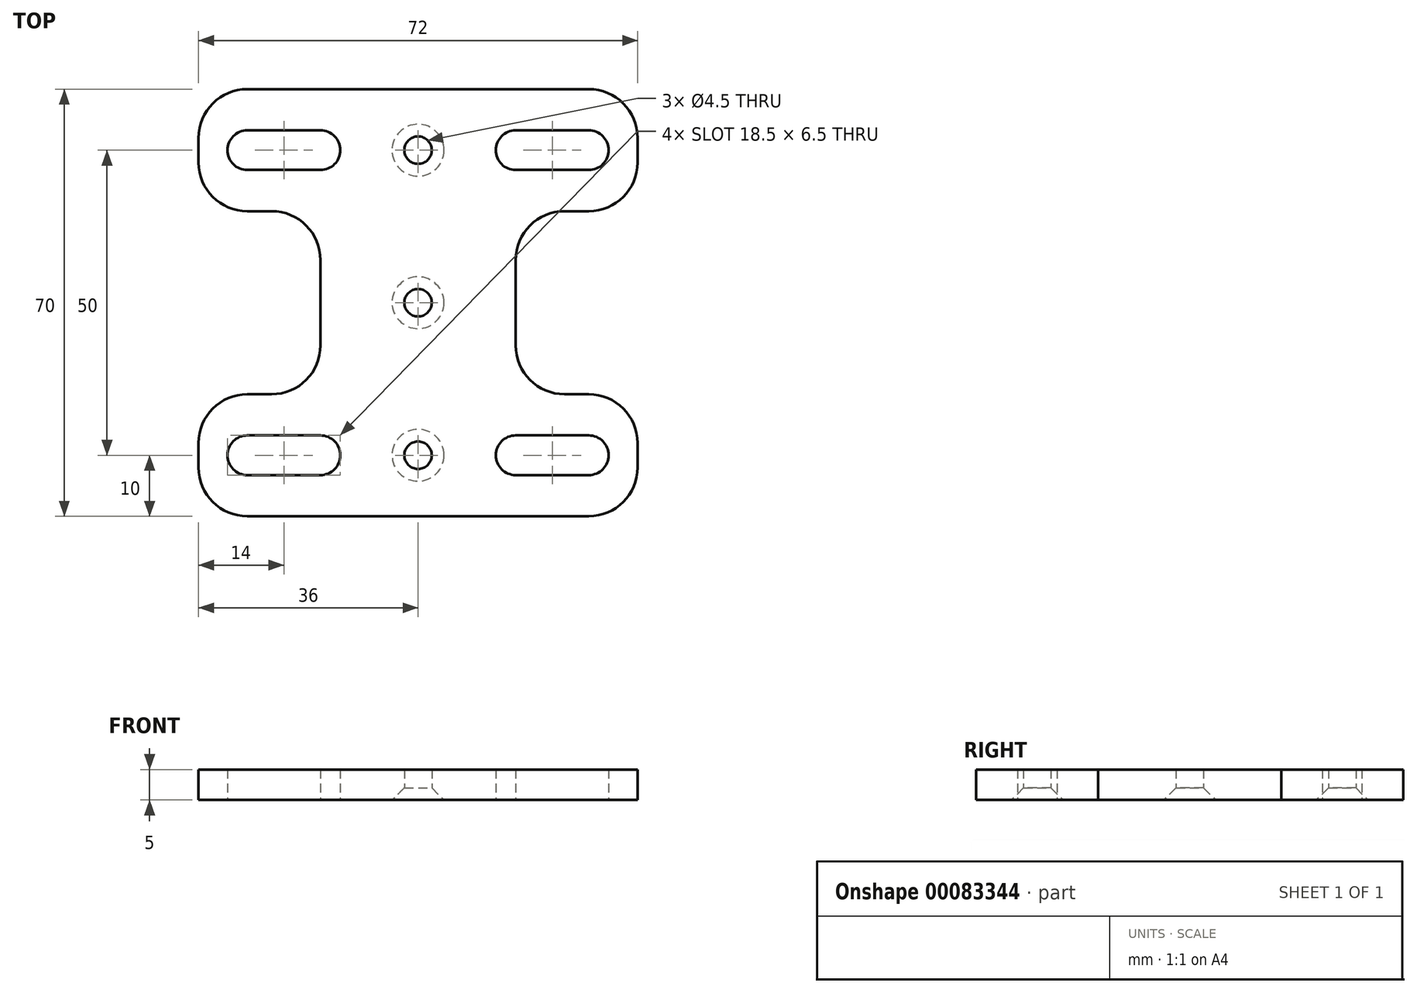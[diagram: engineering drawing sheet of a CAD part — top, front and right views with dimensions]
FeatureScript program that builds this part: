
annotation { "Feature Type Name" : "Feature", "Feature Type Description" : "" }
export const myFeature = defineFeature(function(context is Context, id is Id, definition is map)
    precondition{}
    {
        {
            var Q0;
            Q0=qCreatedBy(makeId("Front.planeOp"),FACE);
            var sketch = newSketch(context, id + "F0", { "sketchPlane" : qUnion([Q0])});
            skLineSegment(sketch, "E0", {"start": v(-14.14, 0) * mm, "end": v(0, -14.14) * mm, "construction": true});
            skLineSegment(sketch, "E1", {"start": v(0, -14.14) * mm, "end": v(14.14, 0) * mm, "construction": true});
            skLineSegment(sketch, "E2", {"start": v(14.14, 0) * mm, "end": v(-14.14, 0) * mm, "construction": true});
            skLineSegment(sketch, "E3", {"start": v(-14.14, 0) * mm, "end": v(0, 14.14) * mm, "construction": true});
            skLineSegment(sketch, "E4", {"start": v(0, 14.14) * mm, "end": v(14.14, 0) * mm, "construction": true});
            skLineSegment(sketch, "E5.0", {"start": v(14.14, -0.03) * mm, "end": v(-14.14, -0.03) * mm, "construction": true});
            skSolve(sketch);
        }
        {
            var Q0;
            Q0=qCreatedBy(makeId("Top.planeOp"),FACE);
            var sketch = newSketch(context, id + "F1", { "sketchPlane" : qUnion([Q0])});
            skLineSegment(sketch, "E6.bottom", {"start": v(-16, 25) * mm, "end": v(16, 25) * mm, "construction": true});
            skLineSegment(sketch, "E6.top", {"start": v(-16, -25) * mm, "end": v(16, -25) * mm, "construction": true});
            skLineSegment(sketch, "E6.left", {"start": v(-16, 25) * mm, "end": v(-16, -25) * mm, "construction": true});
            skLineSegment(sketch, "E6.right", {"start": v(16, 25) * mm, "end": v(16, -25) * mm, "construction": true});
            skCircle(sketch, "E7", {"center": v(-16, 25) * mm, "radius": 3.25 * mm});
            skCircle(sketch, "E8", {"center": v(16, 25) * mm, "radius": 3.25 * mm});
            skCircle(sketch, "E9", {"center": v(-16, -25) * mm, "radius": 3.25 * mm});
            skCircle(sketch, "E10", {"center": v(16, -25) * mm, "radius": 3.25 * mm});
            skLineSegment(sketch, "E11", {"start": v(-36, 35) * mm, "end": v(36, 35) * mm});
            skLineSegment(sketch, "E12", {"start": v(36, 35) * mm, "end": v(36, -35) * mm});
            skLineSegment(sketch, "E13", {"start": v(36, -35) * mm, "end": v(-36, -35) * mm});
            skLineSegment(sketch, "E14", {"start": v(-36, 35) * mm, "end": v(-36, -35) * mm});
            skLineSegment(sketch, "E15", {"start": v(-16, 25) * mm, "end": v(-28, 25) * mm, "construction": true});
            skLineSegment(sketch, "E16", {"start": v(-16, -25) * mm, "end": v(-28, -25) * mm, "construction": true});
            skLineSegment(sketch, "E17", {"start": v(16, -25) * mm, "end": v(28, -25) * mm, "construction": true});
            skLineSegment(sketch, "E18", {"start": v(16, 25) * mm, "end": v(28, 25) * mm, "construction": true});
            skCircle(sketch, "E19", {"center": v(-28, 25) * mm, "radius": 3.25 * mm});
            skCircle(sketch, "E20", {"center": v(-28, -25) * mm, "radius": 3.25 * mm});
            skCircle(sketch, "E21", {"center": v(28, -25) * mm, "radius": 3.25 * mm});
            skCircle(sketch, "E22", {"center": v(28, 25) * mm, "radius": 3.25 * mm});
            skLineSegment(sketch, "E23", {"start": v(-16, 28.25) * mm, "end": v(-28, 28.25) * mm});
            skLineSegment(sketch, "E24", {"start": v(-28, 21.75) * mm, "end": v(-16, 21.75) * mm});
            skLineSegment(sketch, "E25", {"start": v(-28, -21.75) * mm, "end": v(-16, -21.75) * mm});
            skLineSegment(sketch, "E26", {"start": v(-16, -28.25) * mm, "end": v(-28, -28.25) * mm});
            skLineSegment(sketch, "E27", {"start": v(28, -21.75) * mm, "end": v(16, -21.75) * mm});
            skLineSegment(sketch, "E28", {"start": v(16, -28.25) * mm, "end": v(28, -28.25) * mm});
            skLineSegment(sketch, "E29", {"start": v(28, 28.25) * mm, "end": v(16, 28.25) * mm});
            skLineSegment(sketch, "E30", {"start": v(16, 21.75) * mm, "end": v(28, 21.75) * mm});
            skLineSegment(sketch, "E31", {"start": v(0, 35) * mm, "end": v(-12.5, 35) * mm, "construction": true});
            skLineSegment(sketch, "E32", {"start": v(-12.5, 35) * mm, "end": v(-22, 35) * mm, "construction": true});
            skCircle(sketch, "E33", {"center": v(-22, 35) * mm, "radius": 9.5 * mm, "construction": true});
            skPoint(sketch, "E34", {"position": v(0, 25) * mm});
            skPoint(sketch, "E35", {"position": v(0, -25) * mm});
            skPoint(sketch, "E36", {"position": v(0, 0) * mm});
            skLineSegment(sketch, "E37", {"start": v(36, 15) * mm, "end": v(16, 15) * mm});
            skLineSegment(sketch, "E38", {"start": v(16, 15) * mm, "end": v(16, -15) * mm});
            skLineSegment(sketch, "E39", {"start": v(16, -15) * mm, "end": v(36, -15) * mm});
            skLineSegment(sketch, "E40", {"start": v(-36, 15) * mm, "end": v(-16, 15) * mm});
            skLineSegment(sketch, "E41", {"start": v(-16, 15) * mm, "end": v(-16, -15) * mm});
            skLineSegment(sketch, "E42", {"start": v(-16, -15) * mm, "end": v(-36, -15) * mm});
            skSolve(sketch);
        }
        {
            var Q0;
            Q0=makeQuery(id+"F1.imprint","IMPRINT",FACE,{"disambiguationData":[TD([[makeQuery(id+"F1.imprint","IMPRINT",EDGE,{"derivedFrom":sQuery(id+"F1.wireOp",EDGE,"E11")}),-1.0]])]});
            extrude(context, id + "F2", {"entities" : qUnion([Q0]), "depth" : 5 * mm});
        }
        {
            var Q0;
            Q0=sQuery(id+"F1.wireOp",VERTEX,"E34");
            var Q1;
            Q1=sQuery(id+"F1.wireOp",VERTEX,"E36");
            var Q2;
            Q2=sQuery(id+"F1.wireOp",VERTEX,"E35");
            var Q3;
            Q3=makeQuery(id+"F2.opExtrude","SWEPT_BODY",BODY,{"disambiguationData":[OSD([sQuery(id+"F1.wireOp",EDGE,"E7"),sQuery(id+"F1.wireOp",EDGE,"E8"),sQuery(id+"F1.wireOp",EDGE,"E9"),sQuery(id+"F1.wireOp",EDGE,"E10"),sQuery(id+"F1.wireOp",EDGE,"E11"),sQuery(id+"F1.wireOp",EDGE,"E12"),sQuery(id+"F1.wireOp",EDGE,"E13"),sQuery(id+"F1.wireOp",EDGE,"E14"),sQuery(id+"F1.wireOp",EDGE,"E19"),sQuery(id+"F1.wireOp",EDGE,"E20"),sQuery(id+"F1.wireOp",EDGE,"E21"),sQuery(id+"F1.wireOp",EDGE,"E22"),sQuery(id+"F1.wireOp",EDGE,"E23"),sQuery(id+"F1.wireOp",EDGE,"E24"),sQuery(id+"F1.wireOp",EDGE,"E25"),sQuery(id+"F1.wireOp",EDGE,"E26"),sQuery(id+"F1.wireOp",EDGE,"E27"),sQuery(id+"F1.wireOp",EDGE,"E28"),sQuery(id+"F1.wireOp",EDGE,"E29"),sQuery(id+"F1.wireOp",EDGE,"E30")])]});
            hole(context, id + "F3", {"style" : HoleStyle.C_SINK, "endStyle" : HoleEndStyle.THROUGH, "oppositeDirection" : true, "holeDiameter" : 4.5 * mm, "cSinkDiameter" : 8.5 * mm, "cSinkAngle" : 90 * degree, "locations" : qUnion([Q0, Q1, Q2]), "scope" : qUnion([Q3]), "isTappedThrough" : true});
        }
        {
            var Q0;
            Q0=makeQuery(id+"F2.opExtrude","SWEPT_EDGE",EDGE,{"disambiguationData":[OSD([sQuery(id+"F1.wireOp",EDGE,"E11"),sQuery(id+"F1.wireOp",EDGE,"E14")])]});
            var Q1;
            Q1=makeQuery(id+"F2.opExtrude","SWEPT_EDGE",EDGE,{"disambiguationData":[OSD([sQuery(id+"F1.wireOp",EDGE,"E14"),sQuery(id+"F1.wireOp",EDGE,"E42")])]});
            var Q2;
            Q2=makeQuery(id+"F2.opExtrude","SWEPT_EDGE",EDGE,{"disambiguationData":[OSD([sQuery(id+"F1.wireOp",EDGE,"E13"),sQuery(id+"F1.wireOp",EDGE,"E14")])]});
            var Q3;
            Q3=makeQuery(id+"F2.opExtrude","SWEPT_EDGE",EDGE,{"disambiguationData":[OSD([sQuery(id+"F1.wireOp",EDGE,"E12"),sQuery(id+"F1.wireOp",EDGE,"E39")])]});
            var Q4;
            Q4=makeQuery(id+"F2.opExtrude","SWEPT_EDGE",EDGE,{"disambiguationData":[OSD([sQuery(id+"F1.wireOp",EDGE,"E12"),sQuery(id+"F1.wireOp",EDGE,"E13")])]});
            var Q5;
            Q5=makeQuery(id+"F2.opExtrude","SWEPT_EDGE",EDGE,{"disambiguationData":[OSD([sQuery(id+"F1.wireOp",EDGE,"E12"),sQuery(id+"F1.wireOp",EDGE,"E37")])]});
            var Q6;
            Q6=makeQuery(id+"F2.opExtrude","SWEPT_EDGE",EDGE,{"disambiguationData":[OSD([sQuery(id+"F1.wireOp",EDGE,"E11"),sQuery(id+"F1.wireOp",EDGE,"E12")])]});
            var Q7;
            Q7=makeQuery(id+"F2.opExtrude","SWEPT_EDGE",EDGE,{"disambiguationData":[OSD([sQuery(id+"F1.wireOp",EDGE,"E41"),sQuery(id+"F1.wireOp",EDGE,"E42")])]});
            var Q8;
            Q8=makeQuery(id+"F2.opExtrude","SWEPT_EDGE",EDGE,{"disambiguationData":[OSD([sQuery(id+"F1.wireOp",EDGE,"E40"),sQuery(id+"F1.wireOp",EDGE,"E41")])]});
            var Q9;
            Q9=makeQuery(id+"F2.opExtrude","SWEPT_EDGE",EDGE,{"disambiguationData":[OSD([sQuery(id+"F1.wireOp",EDGE,"E37"),sQuery(id+"F1.wireOp",EDGE,"E38")])]});
            var Q10;
            Q10=makeQuery(id+"F2.opExtrude","SWEPT_EDGE",EDGE,{"disambiguationData":[OSD([sQuery(id+"F1.wireOp",EDGE,"E38"),sQuery(id+"F1.wireOp",EDGE,"E39")])]});
            var Q11;
            Q11=makeQuery(id+"F2.opExtrude","SWEPT_EDGE",EDGE,{"disambiguationData":[OSD([sQuery(id+"F1.wireOp",EDGE,"E14"),sQuery(id+"F1.wireOp",EDGE,"E40")])]});
            fillet(context, id + "F4", {"entities" : qUnion([Q0, Q1, Q2, Q3, Q4, Q5, Q6, Q7, Q8, Q9, Q10, Q11]), "radius" : 8 * mm, "tangentPropagation" : true, "allowEdgeOverflow" : false});
        }
    });
